# Revit family: 95800020
name_source: partatom
category: Modelos genéricos
revit_build: Autodesk Revit 2016 (Build: 20150220_1215(x64)
units: mm (PartAtom-declared; Revit-internal decimal feet)

## family parameters
Com base no plano de trabalho = Não
Compartilhado = Não
Corte com vazios quando carregados = Não
Cota do conector redondo = Utilizar diâmetro
Pode hospedar o vergalhão = Não
Ponto de cálculo do ambiente = Não
Sempre na vertical = Sim
Tipo de parte = Normal

## types (1)
- New Vetro Isla 90 - 95800/020
    Comentários de tipos = Ler Manual de Instalação
    Código de montagem = 95800/020
    Descrição = New Vetro Isla 90 - 95800/020
    Desenvolvedor = Factory Cursos & Desenvolvimento
    Fabricante = Tramontina
    Filtro Metalico lávavel = 1
    Filtro de Carvão Ativado = 1 (ambifresh 1)
    Lâmpadas = Leds 4X 1,5 W
    Nivel de Ruido = 73 db
    Numero de Velocidades = 4
    Potencia Elétrica (220 V) = 170 W
    Potencia Maxima = 404 W
    Referencia = 95800/020
    Site do desenvolvedor = www.factorycursos.com.br
    Tensão = 220  [stored 0.721785 ft]
    Tipo de imagem = <Nenhum>
    URL = www.tramontina.com.br
    Vazão Maxima = 890 m3/h

note: [stored X ft] marks values corroborated as IEEE doubles in the binary element streams (Revit-internal decimal feet)
